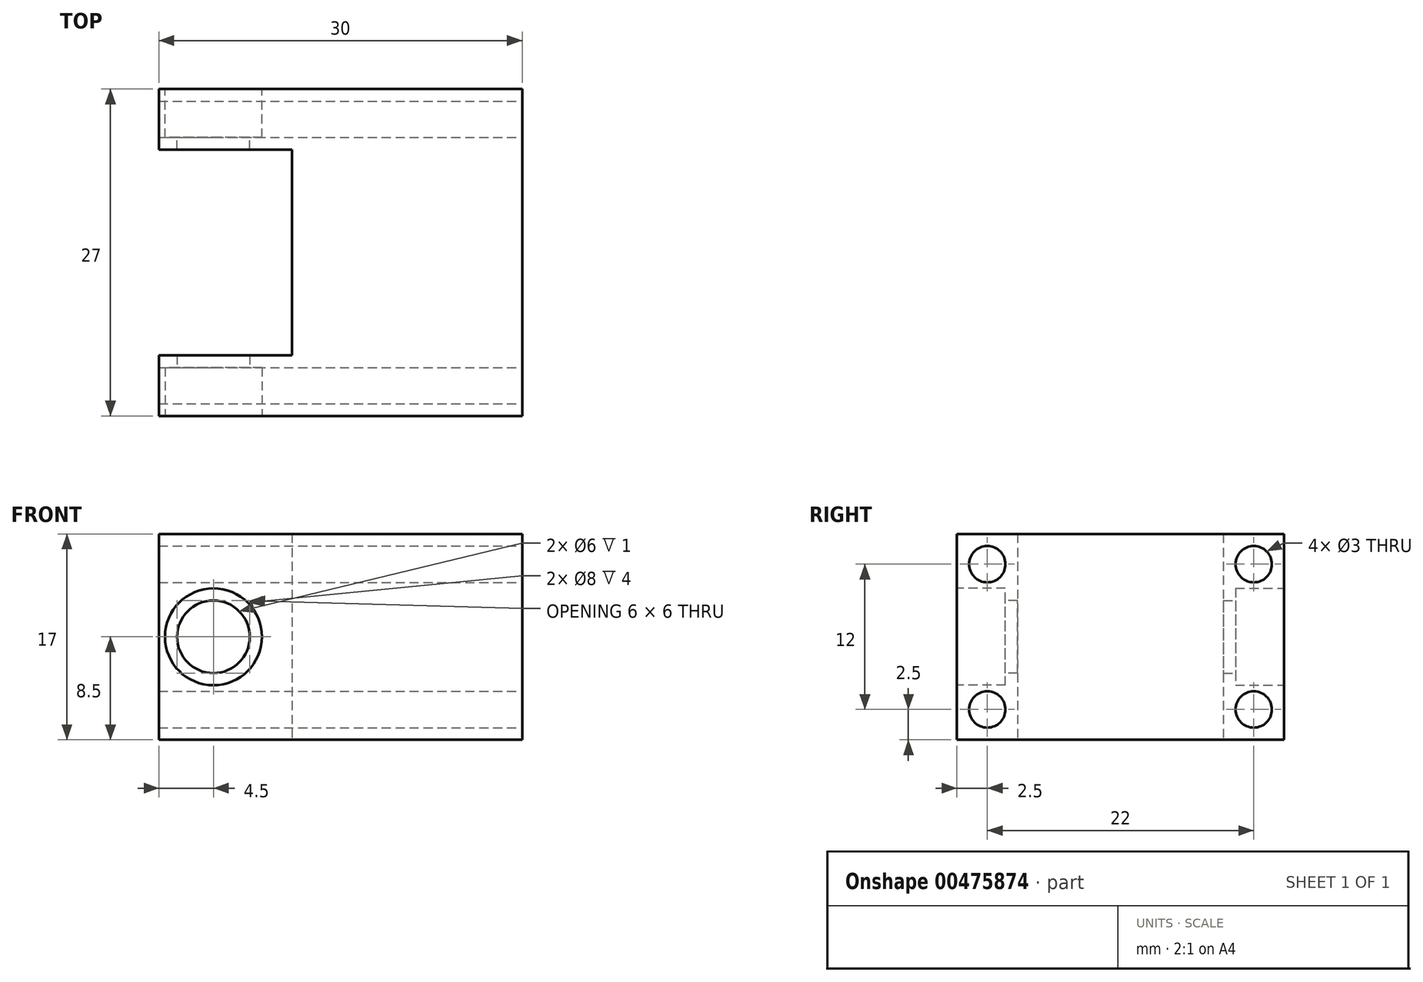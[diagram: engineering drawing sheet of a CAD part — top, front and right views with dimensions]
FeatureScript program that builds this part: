
annotation { "Feature Type Name" : "Feature", "Feature Type Description" : "" }
export const myFeature = defineFeature(function(context is Context, id is Id, definition is map)
    precondition{}
    {
        {
            var Q0;
            Q0=qCreatedBy(makeId("Top.planeOp"),FACE);
            var sketch = newSketch(context, id + "F0", { "sketchPlane" : qUnion([Q0])});
            skLineSegment(sketch, "E0", {"start": v(-11, 13.5) * mm, "end": v(19, 13.5) * mm});
            skLineSegment(sketch, "E1", {"start": v(19, 13.5) * mm, "end": v(19, -13.5) * mm});
            skLineSegment(sketch, "E2", {"start": v(19, -13.5) * mm, "end": v(-11, -13.5) * mm});
            skLineSegment(sketch, "E3", {"start": v(-11, -13.5) * mm, "end": v(-11, -8.5) * mm});
            skLineSegment(sketch, "E4", {"start": v(-11, -8.5) * mm, "end": v(0, -8.5) * mm});
            skLineSegment(sketch, "E5", {"start": v(0, -8.5) * mm, "end": v(0, 8.5) * mm});
            skLineSegment(sketch, "E6", {"start": v(0, 8.5) * mm, "end": v(-11, 8.5) * mm});
            skLineSegment(sketch, "E7", {"start": v(-11, 8.5) * mm, "end": v(-11, 13.5) * mm});
            skSolve(sketch);
        }
        {
            var Q0;
            Q0=makeQuery(id+"F0.imprint","IMPRINT",FACE,{"disambiguationData":[TD([[makeQuery(id+"F0.imprint","IMPRINT",EDGE,{"derivedFrom":sQuery(id+"F0.wireOp",EDGE,"E0")}),-1.0]])]});
            extrude(context, id + "F1", {"entities" : qUnion([Q0]), "endBound" : BoundingType.SYMMETRIC, "depth" : 17 * mm});
        }
        {
            var Q0;
            Q0=makeQuery(id+"F1.opExtrude","SWEPT_FACE",FACE,{"disambiguationData":[OSD([sQuery(id+"F0.wireOp",EDGE,"E2")])]});
            var sketch = newSketch(context, id + "F2", { "sketchPlane" : qUnion([Q0])});
            skCircle(sketch, "E8", {"center": v(-6.5, 0) * mm, "radius": 4 * mm});
            skCircle(sketch, "E9.0", {"center": v(-6.5, 0) * mm, "radius": 3 * mm});
            skSolve(sketch);
        }
        {
            var Q0;
            Q0=makeQuery(id+"F2.imprint","IMPRINT",FACE,{"disambiguationData":[TD([[makeQuery(id+"F2.imprint","IMPRINT",EDGE,{"derivedFrom":sQuery(id+"F2.wireOp",EDGE,"E9.0")}),1.0]])]});
            var Q1;
            Q1=makeQuery(id+"F1.opExtrude","SWEPT_FACE",FACE,{"disambiguationData":[OSD([sQuery(id+"F0.wireOp",EDGE,"E4")])]});
            extrude(context, id + "F3", {"entities" : qUnion([Q0]), "operationType" : NewBodyOperationType.REMOVE, "endBound" : BoundingType.UP_TO_SURFACE, "oppositeDirection" : true, "endBoundEntityFace" : qUnion([Q1]), "depth" : 25 * mm});
        }
        {
            var Q0;
            Q0=makeQuery(id+"F2.imprint","IMPRINT",FACE,{"disambiguationData":[TD([[makeQuery(id+"F2.imprint","IMPRINT",EDGE,{"derivedFrom":sQuery(id+"F2.wireOp",EDGE,"E8")}),1.0]])]});
            extrude(context, id + "F4", {"entities" : qUnion([Q0]), "operationType" : NewBodyOperationType.REMOVE, "oppositeDirection" : true, "depth" : 4 * mm});
        }
        {
            var Q0;
            Q0=makeQuery(id+"F1.opExtrude","SWEPT_FACE",FACE,{"disambiguationData":[OSD([sQuery(id+"F0.wireOp",EDGE,"E0")])]});
            var sketch = newSketch(context, id + "F5", { "sketchPlane" : qUnion([Q0])});
            skCircle(sketch, "E10", {"center": v(6.5, 0) * mm, "radius": 4 * mm});
            skCircle(sketch, "E11.0", {"center": v(6.5, 0) * mm, "radius": 3 * mm});
            skSolve(sketch);
        }
        {
            var Q0;
            Q0=makeQuery(id+"F5.imprint","IMPRINT",FACE,{"disambiguationData":[TD([[makeQuery(id+"F5.imprint","IMPRINT",EDGE,{"derivedFrom":sQuery(id+"F5.wireOp",EDGE,"E11.0")}),1.0]])]});
            var Q1;
            Q1=makeQuery(id+"F1.opExtrude","SWEPT_FACE",FACE,{"disambiguationData":[OSD([sQuery(id+"F0.wireOp",EDGE,"E6")])]});
            extrude(context, id + "F6", {"entities" : qUnion([Q0]), "operationType" : NewBodyOperationType.REMOVE, "endBound" : BoundingType.UP_TO_SURFACE, "oppositeDirection" : true, "endBoundEntityFace" : qUnion([Q1]), "depth" : 25 * mm});
        }
        {
            var Q0;
            Q0=qSketchRegion(id+"F5",true);
            extrude(context, id + "F7", {"entities" : qUnion([Q0]), "operationType" : NewBodyOperationType.REMOVE, "oppositeDirection" : true, "depth" : 4 * mm});
        }
        {
            var Q0;
            Q0=makeQuery(id+"F1.opExtrude","SWEPT_FACE",FACE,{"disambiguationData":[OSD([sQuery(id+"F0.wireOp",EDGE,"E1")])]});
            var sketch = newSketch(context, id + "F8", { "sketchPlane" : qUnion([Q0])});
            skPoint(sketch, "E12", {"position": v(-11, 6) * mm});
            skPoint(sketch, "E13.MirrorP", {"position": v(11, 6) * mm});
            skPoint(sketch, "E14.MirrorP", {"position": v(11, -6) * mm});
            skPoint(sketch, "E15.MirrorP", {"position": v(-11, -6) * mm});
            skSolve(sketch);
        }
        {
            var Q0;
            Q0=sQuery(id+"F8.wireOp",VERTEX,"E12");
            var Q1;
            Q1=sQuery(id+"F8.wireOp",VERTEX,"E15.MirrorP");
            var Q2;
            Q2=sQuery(id+"F8.wireOp",VERTEX,"E14.MirrorP");
            var Q3;
            Q3=sQuery(id+"F8.wireOp",VERTEX,"E13.MirrorP");
            var Q4;
            Q4=makeQuery(id+"F1.opExtrude","SWEPT_BODY",BODY,{"disambiguationData":[OSD([sQuery(id+"F0.wireOp",EDGE,"E0"),sQuery(id+"F0.wireOp",EDGE,"E1"),sQuery(id+"F0.wireOp",EDGE,"E2"),sQuery(id+"F0.wireOp",EDGE,"E3"),sQuery(id+"F0.wireOp",EDGE,"E4"),sQuery(id+"F0.wireOp",EDGE,"E5"),sQuery(id+"F0.wireOp",EDGE,"E6"),sQuery(id+"F0.wireOp",EDGE,"E7")])]});
            hole(context, id + "F9", {"style" : HoleStyle.SIMPLE, "endStyle" : HoleEndStyle.THROUGH, "holeDiameter" : 3 * mm, "isTappedThrough" : true, "tappedDepth" : 12 * mm, "tapClearance" : 3, "locations" : qUnion([Q0, Q1, Q2, Q3]), "scope" : qUnion([Q4])});
        }
    });
